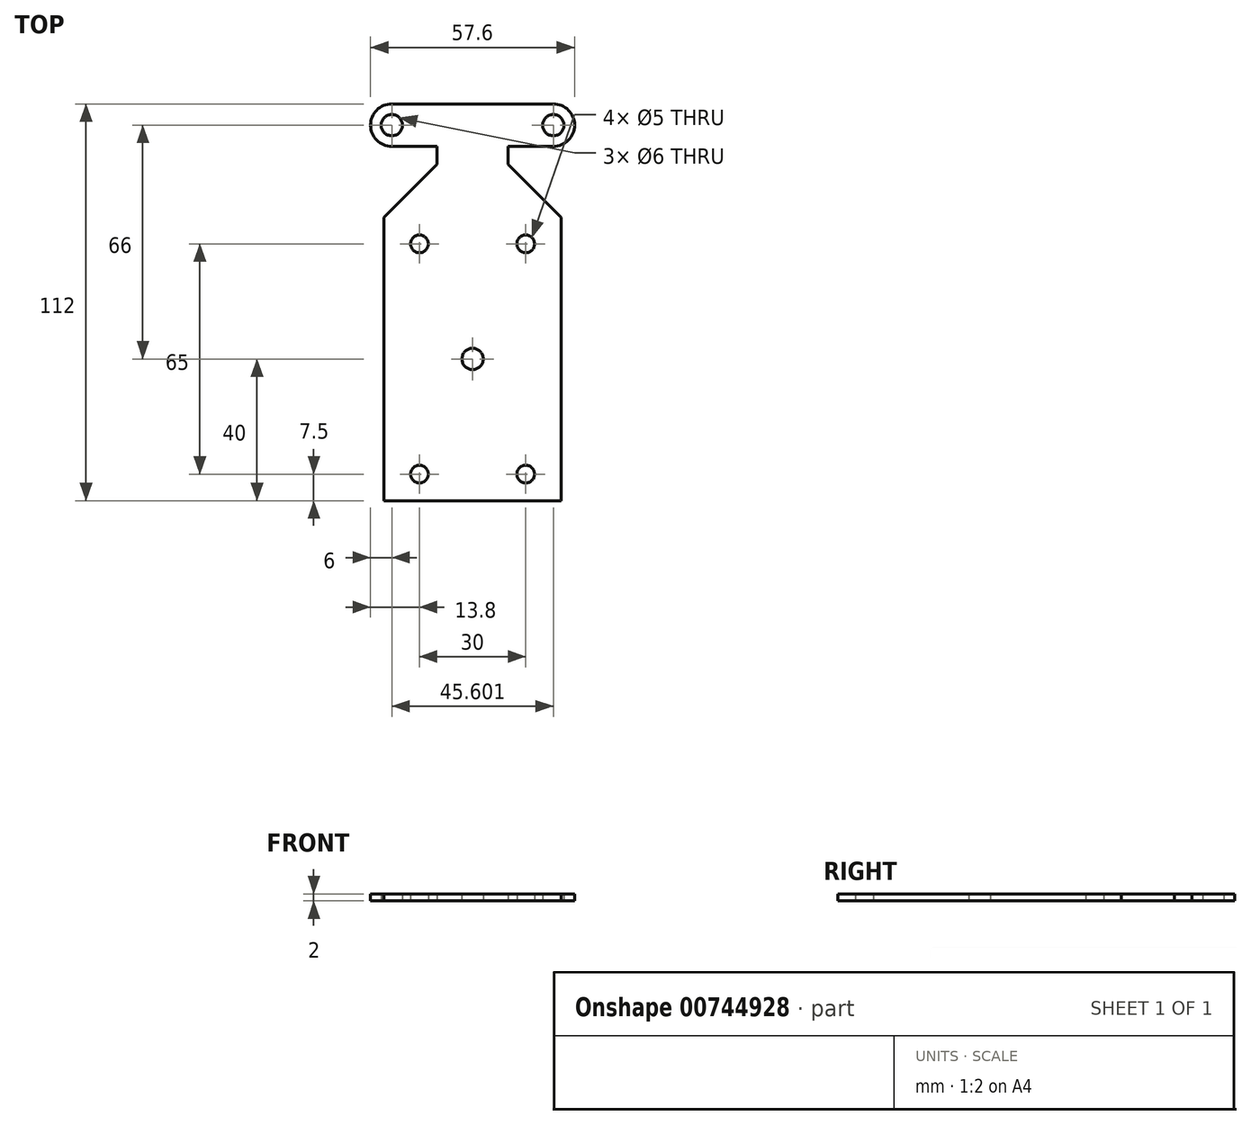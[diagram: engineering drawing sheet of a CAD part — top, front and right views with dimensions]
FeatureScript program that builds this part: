
annotation { "Feature Type Name" : "Feature", "Feature Type Description" : "" }
export const myFeature = defineFeature(function(context is Context, id is Id, definition is map)
    precondition{}
    {
        {
            var Q0;
            Q0=qCreatedBy(makeId("Top.planeOp"),FACE);
            var sketch = newSketch(context, id + "F0", { "sketchPlane" : qUnion([Q0])});
            skLineSegment(sketch, "E0", {"start": v(0, 0) * mm, "end": v(25, 0) * mm});
            skLineSegment(sketch, "E1", {"start": v(25, 0) * mm, "end": v(25, 80) * mm});
            skLineSegment(sketch, "E2", {"start": v(25, 80) * mm, "end": v(10, 95) * mm});
            skLineSegment(sketch, "E3", {"start": v(10, 95) * mm, "end": v(10, 100) * mm});
            skLineSegment(sketch, "E4", {"start": v(10, 100) * mm, "end": v(22.8, 100) * mm});
            skLineSegment(sketch, "E5", {"start": v(22.8, 112) * mm, "end": v(0, 112) * mm});
            skLineSegment(sketch, "E6", {"start": v(0, 112) * mm, "end": v(0, 0) * mm});
            skLineSegment(sketch, "E7", {"start": v(0, 99.66) * mm, "end": v(0, -14.24) * mm, "construction": true});
            skLineSegment(sketch, "E8.MirrorCS", {"start": v(-22.8, 112) * mm, "end": v(0, 112) * mm});
            skLineSegment(sketch, "E9.MirrorCS", {"start": v(-10, 100) * mm, "end": v(-22.8, 100) * mm});
            skLineSegment(sketch, "E10.MirrorCS", {"start": v(-10, 95) * mm, "end": v(-10, 100) * mm});
            skLineSegment(sketch, "E11.MirrorCS", {"start": v(-25, 80) * mm, "end": v(-10, 95) * mm});
            skLineSegment(sketch, "E12.MirrorCS", {"start": v(-25, 0) * mm, "end": v(-25, 80) * mm});
            skLineSegment(sketch, "E13.MirrorCS", {"start": v(0, 0) * mm, "end": v(-25, 0) * mm});
            skArc(sketch, "E14", {"start": v(22.8, 100) * mm, "mid": v(28.8, 106) * mm, "end": v(22.8, 112) * mm});
            skArc(sketch, "E15", {"start": v(-22.8, 112) * mm, "mid": v(-28.8, 106) * mm, "end": v(-22.8, 100) * mm});
            skCircle(sketch, "E16", {"center": v(0, 40) * mm, "radius": 3 * mm});
            skCircle(sketch, "E17", {"center": v(-15, 7.5) * mm, "radius": 2.5 * mm});
            skLineSegment(sketch, "E18", {"start": v(-33.4, 40) * mm, "end": v(36.72, 40) * mm, "construction": true});
            skCircle(sketch, "E19.MirrorC", {"center": v(15, 7.5) * mm, "radius": 2.5 * mm});
            skCircle(sketch, "E20.MirrorC", {"center": v(-15, 72.5) * mm, "radius": 2.5 * mm});
            skCircle(sketch, "E21.MirrorC", {"center": v(15, 72.5) * mm, "radius": 2.5 * mm});
            skCircle(sketch, "E22", {"center": v(-22.8, 106) * mm, "radius": 3 * mm});
            skCircle(sketch, "E23.MirrorC", {"center": v(22.8, 106) * mm, "radius": 3 * mm});
            skLineSegment(sketch, "E24", {"start": v(-10, 100) * mm, "end": v(-10, 112) * mm, "construction": true});
            skLineSegment(sketch, "E25", {"start": v(10, 100) * mm, "end": v(10, 112) * mm, "construction": true});
            skLineSegment(sketch, "E26", {"start": v(-25, 80) * mm, "end": v(25, 80) * mm});
            skLineSegment(sketch, "E27", {"start": v(25, 65) * mm, "end": v(-25, 65) * mm});
            skLineSegment(sketch, "E28", {"start": v(-25, 15) * mm, "end": v(25, 15) * mm});
            skSolve(sketch);
        }
        {
            var Q0;
            Q0 = qSketchRegion(id + "F0", true);
            extrude(context, id + "F1", {"entities" : qUnion([Q0]), "depth" : 2 * mm, "offsetDistance" : 25 * mm});
        }
    });
